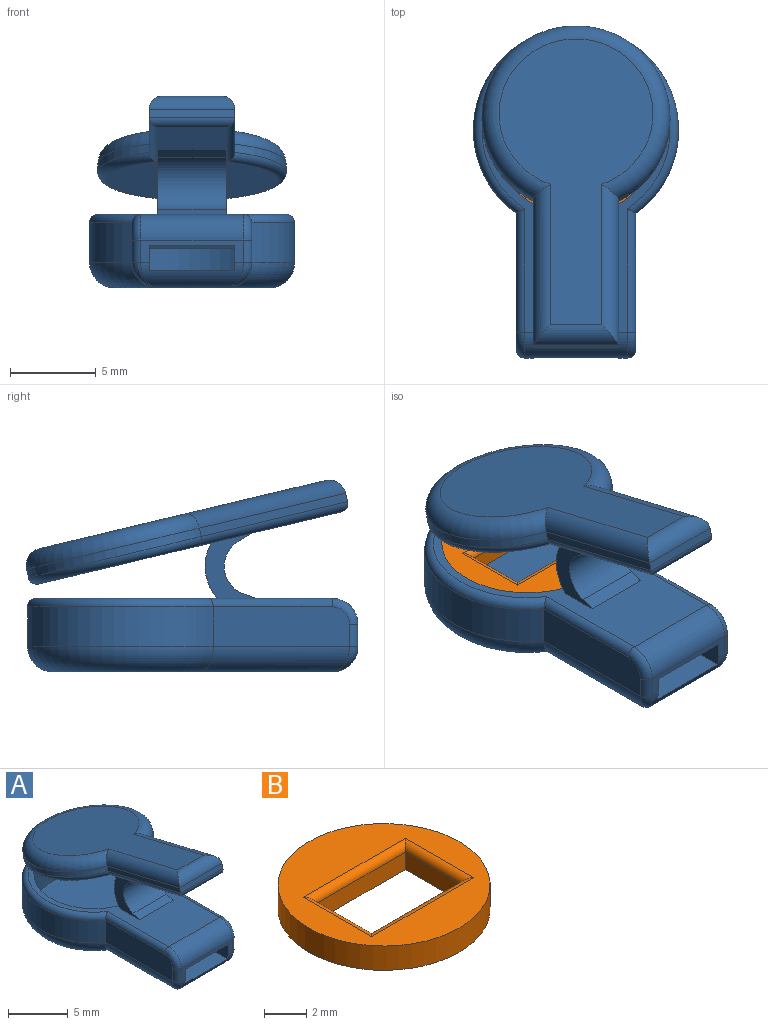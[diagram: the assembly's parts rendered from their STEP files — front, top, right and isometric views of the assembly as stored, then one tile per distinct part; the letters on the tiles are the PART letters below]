
ASSEMBLY  parts=2 mates=1
PART A: 47 faces, bbox 13x20x11.4 mm
  f0: plane 17.33x11mm, normal (0,0,1), area 47.2mm2, adj f10,f16,f20,f21,f22,f27,f28,f29
  f1: plane 10.09x10mm, normal (0,-0.23,-0.97), area 80.6mm2, adj f28,f37,f39,f40
  f2: plane 9x1.5mm, normal (-1,0,0), area 11.8mm2, adj f4,f5,f10,f11,f15,f26
  f3: plane 9x1.5mm, normal (1,0,0), area 11.8mm2, adj f4,f5,f10,f11,f15,f26
  f4: plane 6x1.3mm, normal (0,-1,0), area 2.8mm2, adj f2,f3,f5,f16,f18,f24,f26
  f5: cylinder r=1.5mm len=6mm, axis (-1,0,0), area 9.9mm2, adj f2,f3,f4,f9,f11,f17,f25
  f6: plane 7.96x2.3mm, normal (1,0,0), area 18.1mm2, adj f7,f14,f22,f23,f24
  f7: cylinder r=6mm len=12mm, axis (0,0,1), area 69.5mm2, adj f6,f8,f12,f21
  f8: plane 7.96x2.3mm, normal (-1,0,0), area 18.1mm2, adj f7,f13,f18,f19,f20
  f9: plane 16.33x9mm, normal (0,0,-1), area 93.5mm2, adj f5,f12,f13,f14
  f10: cylinder r=5mm len=10mm, axis (0,0,1), area 96.9mm2, adj f0,f2,f3,f11,f15
  f11: plane 18.24x10mm, normal (0,0,1), area 120.8mm2, adj f2,f3,f5,f10
  f12: torus R=4.5mm, axis (0,0,1), area 66mm2, adj f7,f9,f13,f14
  f13: cylinder r=1.5mm len=8.8mm, axis (0,1,0), area 18.6mm2, adj f8,f9,f12,f17
  f14: cylinder r=1.5mm len=8.8mm, axis (0,-1,0), area 18.6mm2, adj f6,f9,f12,f25
  f15: plane 7.5x5mm, normal (0,0,-1), area 35.2mm2, adj f2,f3,f10,f26
  f16: cylinder r=1.5mm len=6mm, axis (1,0,0), area 14.1mm2, adj f0,f4,f19,f23
  f17: bspline ~1.76x1.5mm, area 1.3mm2, adj f5,f13,f18
  f18: cylinder r=0.5mm len=1.3mm, axis (0,0,1), area 1mm2, adj f4,f8,f17,f19
  f19: torus R=1mm, axis (-1,0,0), area 1.6mm2, adj f8,f16,f18,f20
  f20: cylinder r=0.5mm len=7.22mm, axis (0,-1,0), area 5.5mm2, adj f0,f8,f19,f21
  f21: torus R=5.5mm, axis (0,0,1), area 23.2mm2, adj f0,f7,f20,f22
  f22: cylinder r=0.5mm len=7.22mm, axis (0,1,0), area 5.5mm2, adj f0,f6,f21,f23
  f23: torus R=1mm, axis (-1,0,0), area 1.6mm2, adj f6,f16,f22,f24
  f24: cylinder r=0.5mm len=1.3mm, axis (0,0,-1), area 1mm2, adj f4,f6,f23,f25
  f25: bspline ~1.57x1.5mm, area 1.3mm2, adj f5,f14,f24
  f26: plane 5x1.5mm, normal (0,-0.13,-0.99), area 7.6mm2, adj f2,f3,f4,f15
  f27: plane 3.81x2.96mm, normal (1,0,0), area 4.6mm2, adj f0,f28,f30,f40,f41,f42
  f28: cylinder r=2.82mm len=4mm, axis (1,0,0), area 13.9mm2, adj f0,f1,f27,f29
  f29: plane 3.81x2.96mm, normal (-1,0,0), area 4.6mm2, adj f0,f28,f30,f37,f41,f42
  f30: cylinder r=1.7mm len=4mm, axis (1,0,0), area 15.2mm2, adj f27,f29,f41,f42
  f31: cylinder r=5.5mm len=11mm, axis (0,-0.23,-0.97), area 14.7mm2, adj f32,f34,f39,f45
  f32: plane 8.68x2.53mm, normal (1,0,0), area 4.4mm2, adj f31,f33,f40,f46
  f33: plane 5x0.49mm, normal (0,-0.97,0.23), area 2.5mm2, adj f32,f34,f38,f44
  f34: plane 8.68x2.53mm, normal (-1,0,0), area 4.4mm2, adj f31,f33,f37,f43
  f35: plane 16.73x9mm, normal (0,0.23,0.97), area 88.5mm2, adj f43,f44,f45,f46
  f36: plane 5.23x4mm, normal (0,-0.23,-0.97), area 21.5mm2, adj f37,f38,f40,f42
  f37: cylinder r=0.5mm len=8.98mm, axis (0,0.97,-0.23), area 6.9mm2, adj f1,f29,f34,f36,f38,f39
  f38: cylinder r=0.5mm len=5mm, axis (-1,0,0), area 3.6mm2, adj f33,f36,f37,f40
  f39: torus R=5mm, axis (0,-0.23,-0.97), area 22.5mm2, adj f1,f31,f37,f40
  f40: cylinder r=0.5mm len=8.98mm, axis (0,-0.97,0.23), area 6.9mm2, adj f1,f27,f32,f36,f38,f39
  f41: plane 4x0.74mm, normal (0,-0.35,0.94), area 3.2mm2, adj f0,f27,f29,f30
  f42: plane 4x0.8mm, normal (0,-0.52,-0.86), area 3.8mm2, adj f27,f29,f30,f36
  f43: cylinder r=1mm len=9.43mm, axis (0,-0.97,0.23), area 13.6mm2, adj f34,f35,f44,f45
  f44: cylinder r=1mm len=5mm, axis (1,0,0), area 6.7mm2, adj f33,f35,f43,f46
  f45: torus R=4.5mm, axis (0,-0.23,-0.97), area 43.8mm2, adj f31,f35,f43,f46
  f46: cylinder r=1mm len=9.43mm, axis (0,0.97,-0.23), area 13.6mm2, adj f32,f35,f44,f45
PART B: 11 faces, bbox 10x10x1.4 mm
  f0: plane 3.75x1mm, normal (1,0,0), area 3.8mm2, adj f1,f4,f5,f7
  f1: plane 6x1mm, normal (0,-1,0), area 6mm2, adj f0,f2,f5,f8
  f2: plane 3.75x1mm, normal (-1,0,0), area 3.8mm2, adj f1,f4,f5,f10
  f3: cylinder r=5mm len=10mm, axis (0,0,1), area 44mm2, adj f5,f6
  f4: plane 6x1mm, normal (0,1,0), area 6mm2, adj f0,f2,f5,f9
  f5: plane 10x10mm, normal (0,0,-1), area 56mm2, adj f0,f1,f2,f3,f4
  f6: plane 10x10mm, normal (0,0,1), area 47.6mm2, adj f3,f7,f8,f9,f10
  f7: cylinder r=0.4mm len=4.55mm, axis (0,1,0), area 2.5mm2, adj f0,f6,f8,f9
  f8: cylinder r=0.4mm len=6.8mm, axis (1,0,0), area 4mm2, adj f1,f6,f7,f10
  f9: cylinder r=0.4mm len=6.8mm, axis (-1,0,0), area 4mm2, adj f4,f6,f7,f10
  f10: cylinder r=0.4mm len=4.55mm, axis (0,-1,0), area 2.5mm2, adj f2,f6,f8,f9
PLACE A t=(18.01,-1.36,0.15)mm
PLACE B t=(18.01,-1.36,0.15)mm
MATE slider B.f3 <-> A.f7  axis (0,0,1) through (18.01,-1.36,0.15)mm
